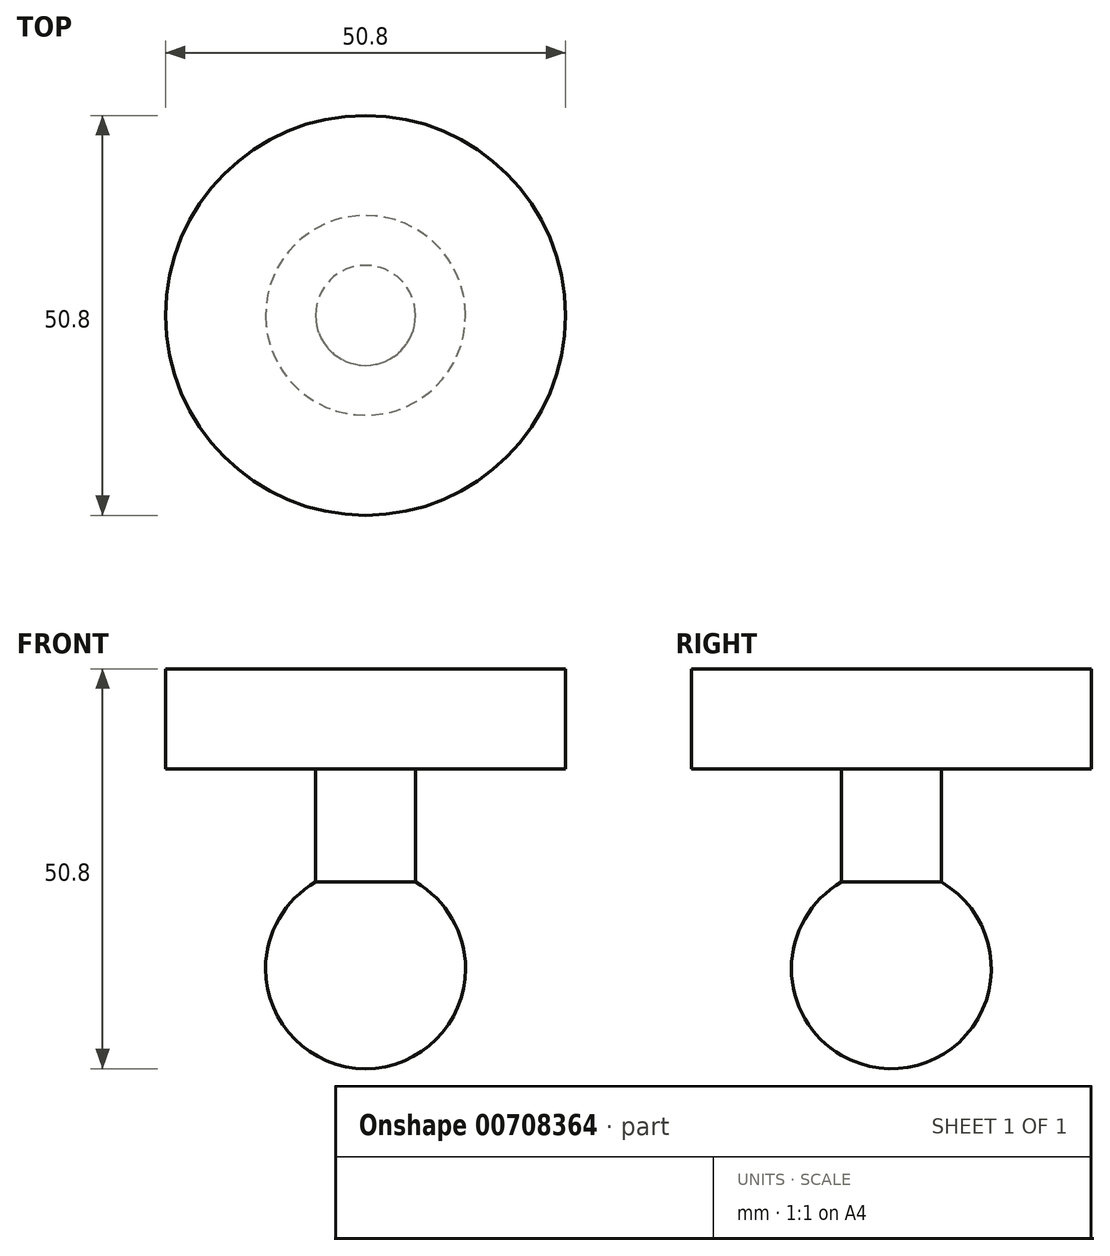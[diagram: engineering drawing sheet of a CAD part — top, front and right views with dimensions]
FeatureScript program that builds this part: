
annotation { "Feature Type Name" : "Feature", "Feature Type Description" : "" }
export const myFeature = defineFeature(function(context is Context, id is Id, definition is map)
    precondition{}
    {
        {
            var Q0;
            Q0=qCreatedBy(makeId("Top.planeOp"),FACE);
            var sketch = newSketch(context, id + "F0", { "sketchPlane" : qUnion([Q0])});
            skArc(sketch, "E0", {"start": v(12.7, 0) * mm, "mid": v(0, -12.7) * mm, "end": v(-12.7, 0) * mm});
            skLineSegment(sketch, "E1", {"start": v(-12.7, 0) * mm, "end": v(12.7, 0) * mm});
            skSolve(sketch);
        }
        {
            var Q0;
            Q0 = qSketchRegion(id + "F0", true);
            var Q1;
            Q1=sQuery(id+"F0.wireOp",EDGE,"E1");
            revolve(context, id + "F1", {"surfaceOperationType" : NewSurfaceOperationType.NEW, "entities" : qUnion([Q0]), "axis" : qUnion([Q1]), "revolveType" : RevolveType.FULL});
        }
        {
            var Q0;
            Q0=qCreatedBy(makeId("Top.planeOp"),FACE);
            var sketch = newSketch(context, id + "F2", { "sketchPlane" : qUnion([Q0])});
            skCircle(sketch, "E2", {"center": v(0, 0) * mm, "radius": 6.35 * mm});
            skSolve(sketch);
        }
        {
            var Q0;
            Q0 = qSketchRegion(id + "F2", true);
            extrude(context, id + "F3", {"entities" : qUnion([Q0]), "operationType" : NewBodyOperationType.ADD, "depth" : 25.4 * mm, "offsetDistance" : 25.4 * mm});
        }
        {
            var Q0;
            Q0=makeQuery(id+"F3.opExtrude","CAP_FACE",FACE,{"disambiguationData":[OSD([sQuery(id+"F2.wireOp",EDGE,"E2")])],"isStart":false});
            var sketch = newSketch(context, id + "F4", { "sketchPlane" : qUnion([Q0])});
            skCircle(sketch, "E3", {"center": v(0, 0) * mm, "radius": 25.4 * mm});
            skSolve(sketch);
        }
        {
            var Q0;
            Q0 = qSketchRegion(id + "F4", true);
            extrude(context, id + "F5", {"entities" : qUnion([Q0]), "operationType" : NewBodyOperationType.ADD, "depth" : 12.7 * mm, "offsetDistance" : 25.4 * mm});
        }
    });
